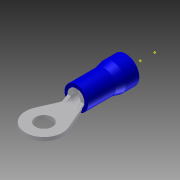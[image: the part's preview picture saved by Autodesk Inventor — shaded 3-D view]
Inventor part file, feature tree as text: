
AUTODESK INVENTOR PART (.ipt)
format: ipt  version: 2011 (Build 150239000, 239)  size: 174,592 bytes
history: native  units: mm
features: other x4, plane x2, imported_body x1, sketch x1
ambient origin geometry x8: Origin, YZ Plane, XZ Plane, XY Plane, X Axis, Y Axis, Z Axis, Center Point
bodies: Solid1 (feature_tree)
feature tree (8):
  imported_body  "Base1"
  sketch  "Sketch1"  dims[d0=3.175mm d1=6.35mm]
  other  "Work Point2"
  other  "Work Point3"
  plane  "Work Plane1"
  other  "Work Axis1"
  plane  "Work Plane2"
  other  "Work Axis2"
